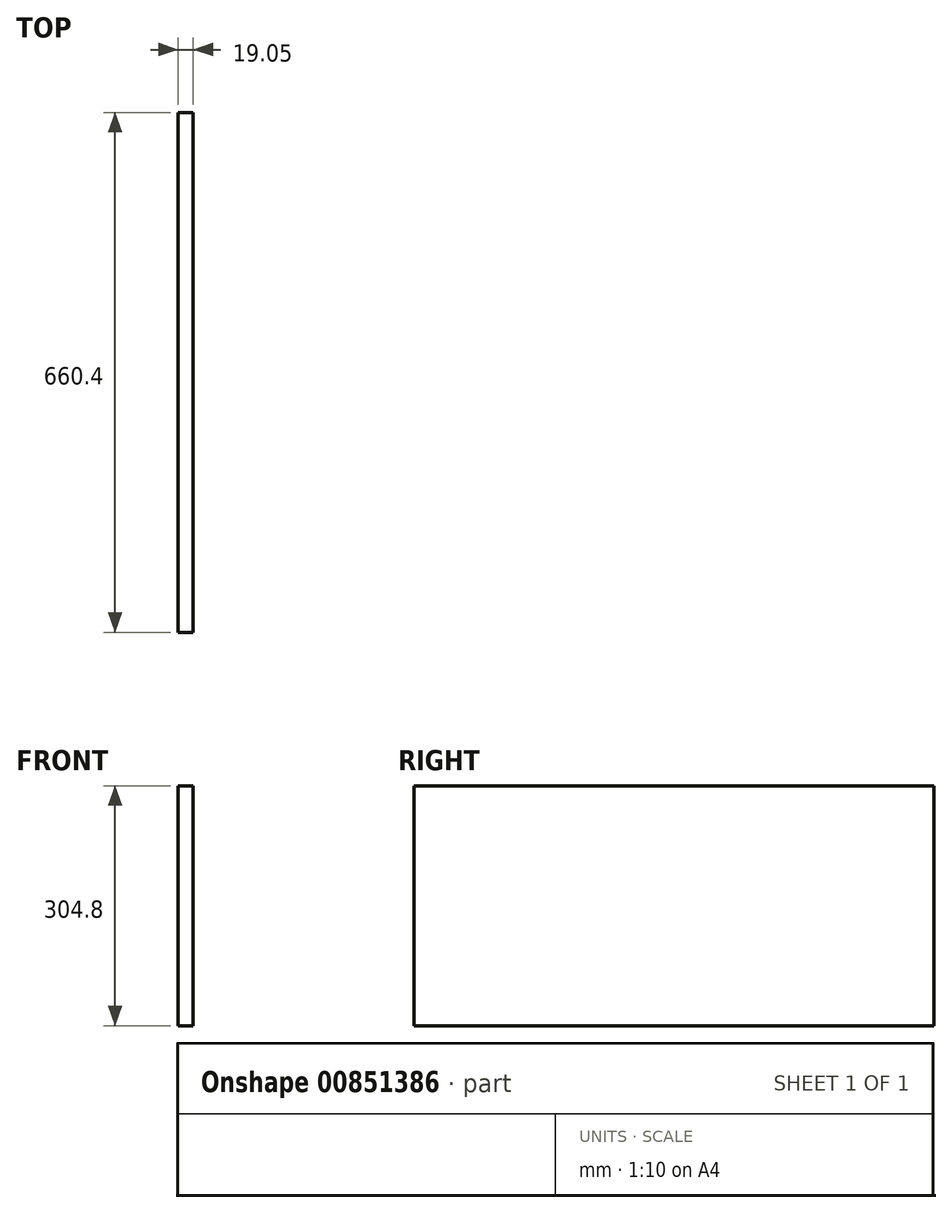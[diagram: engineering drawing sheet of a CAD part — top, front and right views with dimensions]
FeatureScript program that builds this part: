
annotation { "Feature Type Name" : "Feature", "Feature Type Description" : "" }
export const myFeature = defineFeature(function(context is Context, id is Id, definition is map)
    precondition{}
    {
        {
            var Q0;
            Q0=qCreatedBy(makeId("Front.planeOp"),FACE);
            var sketch = newSketch(context, id + "F0", { "sketchPlane" : qUnion([Q0])});
            skLineSegment(sketch, "E0.bottom", {"start": v(-64.37, 284.23) * mm, "end": v(-45.32, 284.23) * mm});
            skLineSegment(sketch, "E0.top", {"start": v(-64.37, -20.57) * mm, "end": v(-45.32, -20.57) * mm});
            skLineSegment(sketch, "E0.left", {"start": v(-64.37, 284.23) * mm, "end": v(-64.37, -20.57) * mm});
            skLineSegment(sketch, "E0.right", {"start": v(-45.32, 284.23) * mm, "end": v(-45.32, -20.57) * mm});
            skSolve(sketch);
        }
        {
            var Q0;
            Q0 = qSketchRegion(id + "F0", true);
            extrude(context, id + "F1", {"entities" : qUnion([Q0]), "depth" : 660.4 * mm, "offsetDistance" : 25.4 * mm});
        }
    });
